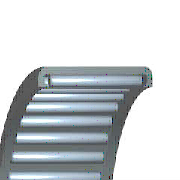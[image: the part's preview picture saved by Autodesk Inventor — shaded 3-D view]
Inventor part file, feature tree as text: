
AUTODESK INVENTOR PART (.ipt)
format: ipt  version: 2016 (Build 200138000, 138)  size: 291,840 bytes
history: native  units: mm (DEFAULTED — no unit token found)
features: sketch x1, other x1, pattern_circular x1
ambient origin geometry x8: Origin, YZ Plane, XZ Plane, XY Plane, X Axis, Y Axis, Z Axis, Center Point
bodies: Solid1 (feature_tree), Body (feature_tree)
feature tree (3):
  sketch  "Sketch"  dims[d36=90.0deg d0=1.25mm d1=0.25mm d39=90.0deg d2=170.0mm d3=360.0deg d4=0.0mm d5=0.0mm d6=1.4mm d7=0.0mm d8=10.0mm d9=14.0mm d10=11.0mm d11=12.0mm d12=1.0mm d13=1.9mm d14=7.0mm d57=0.0mm d58=0.0mm]
  other  "Roller"
  pattern_circular  "Rollers"  [2 undecoded]
note: 2 required parameter values undecoded (feature->parameter linkage not recoverable at this tier; creation-order binding heuristic only, values carry confidence <= 0.55)
